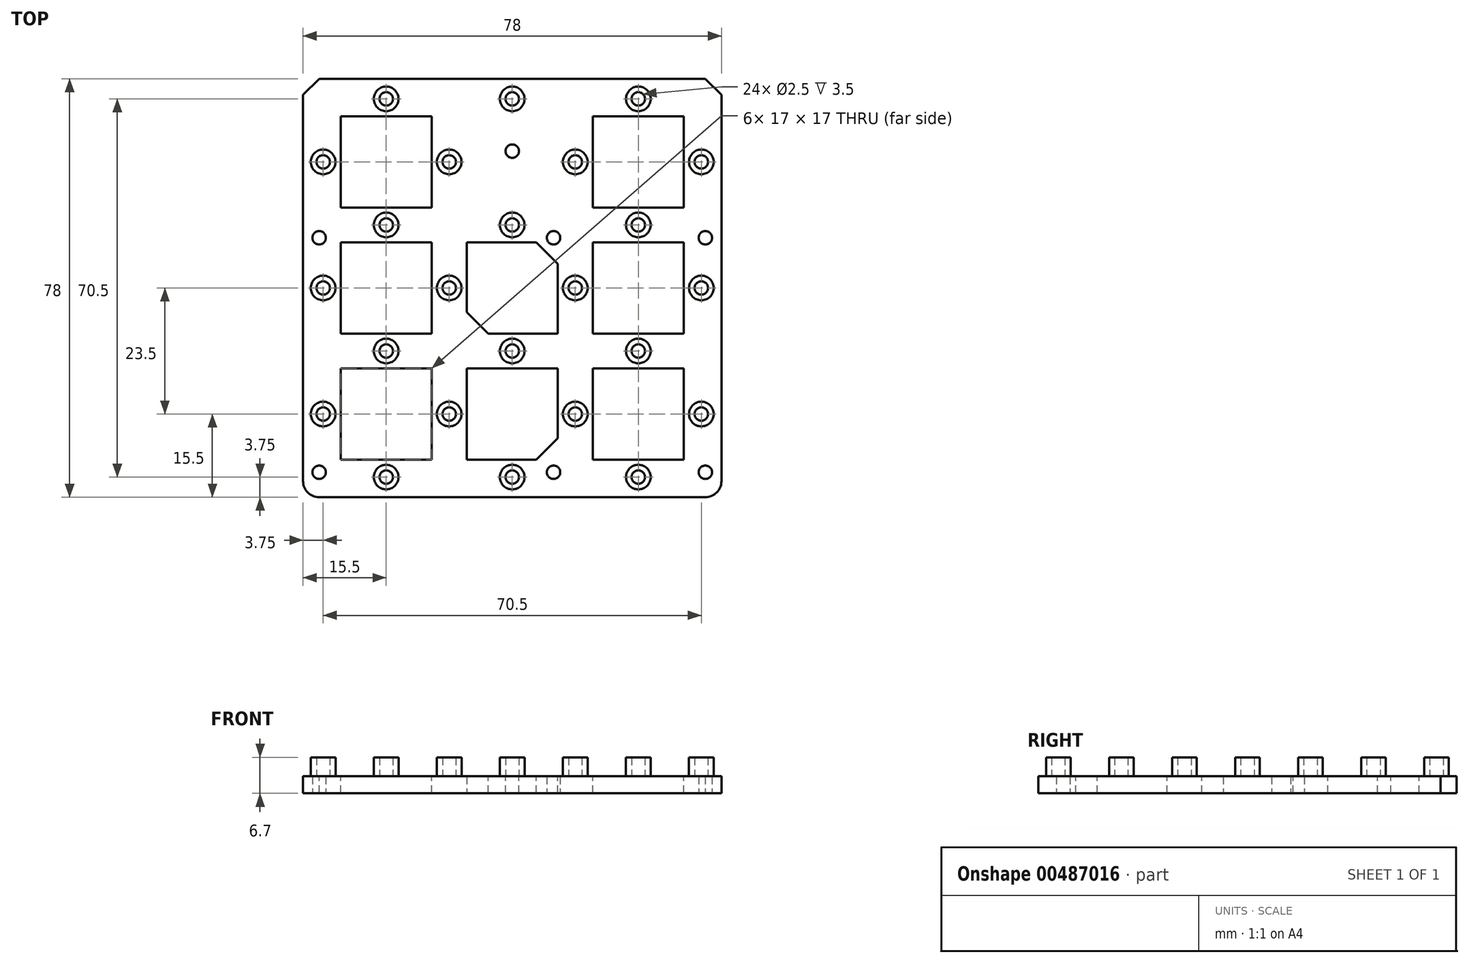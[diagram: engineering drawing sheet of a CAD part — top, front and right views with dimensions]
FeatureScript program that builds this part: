
annotation { "Feature Type Name" : "Feature", "Feature Type Description" : "" }
export const myFeature = defineFeature(function(context is Context, id is Id, definition is map)
    precondition{}
    {
        {
            assignVariable(context, id + "F0", {"name" : "Grosor", "anyValue" : 3.2});
        }
        {
            var Q0;
            Q0=qCreatedBy(makeId("Top.planeOp"),FACE);
            var sketch = newSketch(context, id + "F1", { "sketchPlane" : qUnion([Q0])});
            skLineSegment(sketch, "E0", {"start": v(0, 0) * mm, "end": v(0, 0) * mm});
            skLineSegment(sketch, "E1", {"start": v(0, 0) * mm, "end": v(0, -12.5) * mm, "construction": true});
            skLineSegment(sketch, "E2.bottom", {"start": v(-36, -34.35) * mm, "end": v(36, -34.35) * mm, "construction": true});
            skLineSegment(sketch, "E2.top", {"start": v(-36, 9.35) * mm, "end": v(36, 9.35) * mm, "construction": true});
            skLineSegment(sketch, "E2.left", {"start": v(-36, -34.35) * mm, "end": v(-36, 9.35) * mm, "construction": true});
            skLineSegment(sketch, "E2.right", {"start": v(36, -34.35) * mm, "end": v(36, 9.35) * mm, "construction": true});
            skPoint(sketch, "E2.middle", {"position": v(0, -12.5) * mm});
            skLineSegment(sketch, "E3.bottom", {"start": v(39, 12) * mm, "end": v(-39, 12) * mm, "construction": true});
            skLineSegment(sketch, "E3.top", {"start": v(39, -37) * mm, "end": v(-39, -37) * mm, "construction": true});
            skLineSegment(sketch, "E3.left", {"start": v(39, 12) * mm, "end": v(39, -37) * mm, "construction": true});
            skLineSegment(sketch, "E3.right", {"start": v(-39, 12) * mm, "end": v(-39, -37) * mm, "construction": true});
            skCircle(sketch, "E4", {"center": v(-36, 9.35) * mm, "radius": 1.25 * mm});
            skCircle(sketch, "E5", {"center": v(36, 9.35) * mm, "radius": 1.25 * mm});
            skCircle(sketch, "E6", {"center": v(36, -34.35) * mm, "radius": 1.25 * mm});
            skCircle(sketch, "E7", {"center": v(-36, -34.35) * mm, "radius": 1.25 * mm});
            skCircle(sketch, "E8", {"center": v(-36, -34.35) * mm, "radius": 2.3 * mm});
            skCircle(sketch, "E9", {"center": v(36, -34.35) * mm, "radius": 2.3 * mm});
            skCircle(sketch, "E10", {"center": v(36, 9.35) * mm, "radius": 2.3 * mm});
            skCircle(sketch, "E11", {"center": v(-36, 9.35) * mm, "radius": 2.3 * mm});
            skLineSegment(sketch, "E12.bottom", {"start": v(-39, -39) * mm, "end": v(39, -39) * mm});
            skLineSegment(sketch, "E12.top", {"start": v(-39, 39) * mm, "end": v(39, 39) * mm});
            skLineSegment(sketch, "E12.left", {"start": v(-39, -39) * mm, "end": v(-39, 39) * mm});
            skLineSegment(sketch, "E12.right", {"start": v(39, -39) * mm, "end": v(39, 39) * mm});
            skPoint(sketch, "E12.middle", {"position": v(0, 0) * mm});
            skLineSegment(sketch, "E13", {"start": v(-36, -20.87) * mm, "end": v(7.7, -20.87) * mm, "construction": true});
            skLineSegment(sketch, "E14", {"start": v(7.7, -20.87) * mm, "end": v(7.7, -34.35) * mm, "construction": true});
            skLineSegment(sketch, "E15", {"start": v(7.7, -20.87) * mm, "end": v(7.7, 9.35) * mm, "construction": true});
            skCircle(sketch, "E16", {"center": v(7.7, 9.35) * mm, "radius": 1.25 * mm});
            skCircle(sketch, "E17", {"center": v(7.7, -34.35) * mm, "radius": 1.25 * mm});
            skCircle(sketch, "E18", {"center": v(7.7, -34.35) * mm, "radius": 2.3 * mm});
            skCircle(sketch, "E19", {"center": v(7.7, 9.35) * mm, "radius": 2.3 * mm});
            skLineSegment(sketch, "E20", {"start": v(0, 12) * mm, "end": v(0, 39) * mm, "construction": true});
            skCircle(sketch, "E21", {"center": v(0, 25.5) * mm, "radius": 1.25 * mm});
            skSolve(sketch);
        }
        {
            var Q0;
            Q0=qSketchRegion(id+"F1",true);
            var Q1;
            Q1=makeQuery(id+"F1.imprint","IMPRINT",FACE,{"disambiguationData":[TD([[makeQuery(id+"F1.imprint","IMPRINT",EDGE,{"derivedFrom":sQuery(id+"F1.wireOp",EDGE,"E4")}),-1.0]])]});
            var Q2;
            Q2=makeQuery(id+"F1.imprint","IMPRINT",FACE,{"disambiguationData":[TD([[makeQuery(id+"F1.imprint","IMPRINT",EDGE,{"derivedFrom":sQuery(id+"F1.wireOp",EDGE,"E5")}),-1.0]])]});
            var Q3;
            Q3=makeQuery(id+"F1.imprint","IMPRINT",FACE,{"disambiguationData":[TD([[makeQuery(id+"F1.imprint","IMPRINT",EDGE,{"derivedFrom":sQuery(id+"F1.wireOp",EDGE,"E6")}),-1.0]])]});
            var Q4;
            Q4=makeQuery(id+"F1.imprint","IMPRINT",FACE,{"disambiguationData":[TD([[makeQuery(id+"F1.imprint","IMPRINT",EDGE,{"derivedFrom":sQuery(id+"F1.wireOp",EDGE,"E7")}),-1.0]])]});
            var Q5;
            Q5=makeQuery(id+"F1.imprint","IMPRINT",FACE,{"disambiguationData":[TD([[makeQuery(id+"F1.imprint","IMPRINT",EDGE,{"derivedFrom":sQuery(id+"F1.wireOp",EDGE,"E16")}),-1.0]])]});
            var Q6;
            Q6=makeQuery(id+"F1.imprint","IMPRINT",FACE,{"disambiguationData":[TD([[makeQuery(id+"F1.imprint","IMPRINT",EDGE,{"derivedFrom":sQuery(id+"F1.wireOp",EDGE,"E17")}),-1.0]])]});
            var Q7;
            Q7=makeQuery(id+"F1.imprint","IMPRINT",FACE,{"disambiguationData":[TD([[makeQuery(id+"F1.imprint","IMPRINT",EDGE,{"derivedFrom":sQuery(id+"F1.wireOp",EDGE,"E4")}),1.0]])]});
            var Q8;
            Q8=makeQuery(id+"F1.imprint","IMPRINT",FACE,{"disambiguationData":[TD([[makeQuery(id+"F1.imprint","IMPRINT",EDGE,{"derivedFrom":sQuery(id+"F1.wireOp",EDGE,"E16")}),1.0]])]});
            var Q9;
            Q9=makeQuery(id+"F1.imprint","IMPRINT",FACE,{"disambiguationData":[TD([[makeQuery(id+"F1.imprint","IMPRINT",EDGE,{"derivedFrom":sQuery(id+"F1.wireOp",EDGE,"E5")}),1.0]])]});
            var Q10;
            Q10=makeQuery(id+"F1.imprint","IMPRINT",FACE,{"disambiguationData":[TD([[makeQuery(id+"F1.imprint","IMPRINT",EDGE,{"derivedFrom":sQuery(id+"F1.wireOp",EDGE,"E7")}),1.0]])]});
            var Q11;
            Q11=makeQuery(id+"F1.imprint","IMPRINT",FACE,{"disambiguationData":[TD([[makeQuery(id+"F1.imprint","IMPRINT",EDGE,{"derivedFrom":sQuery(id+"F1.wireOp",EDGE,"E17")}),1.0]])]});
            var Q12;
            Q12=makeQuery(id+"F1.imprint","IMPRINT",FACE,{"disambiguationData":[TD([[makeQuery(id+"F1.imprint","IMPRINT",EDGE,{"derivedFrom":sQuery(id+"F1.wireOp",EDGE,"E6")}),1.0]])]});
            extrude(context, id + "F2", {"entities" : qUnion([Q0, Q1, Q2, Q3, Q4, Q5, Q6, Q7, Q8, Q9, Q10, Q11, Q12]), "endBound" : BoundingType.SYMMETRIC, "oppositeDirection" : true, "depth" : (getVariable(context, 'Grosor')) * mm});
        }
        {
            var Q0;
            Q0=qCreatedBy(makeId("Top.planeOp"),FACE);
            var sketch = newSketch(context, id + "F3", { "sketchPlane" : qUnion([Q0])});
            skLineSegment(sketch, "E22", {"start": v(0, 0) * mm, "end": v(-11.75, 0) * mm, "construction": true});
            skLineSegment(sketch, "E23", {"start": v(-11.75, 0) * mm, "end": v(-35.25, 0) * mm, "construction": true});
            skLineSegment(sketch, "E24.bottom", {"start": v(0, 11.75) * mm, "end": v(-23.5, 11.75) * mm, "construction": true});
            skLineSegment(sketch, "E24.top", {"start": v(0, -11.75) * mm, "end": v(-23.5, -11.75) * mm, "construction": true});
            skLineSegment(sketch, "E24.left", {"start": v(0, 11.75) * mm, "end": v(0, -11.75) * mm, "construction": true});
            skLineSegment(sketch, "E24.right", {"start": v(-23.5, 11.75) * mm, "end": v(-23.5, -11.75) * mm, "construction": true});
            skPoint(sketch, "E24.middle", {"position": v(-11.75, 0) * mm});
            skLineSegment(sketch, "E25", {"start": v(0, 0) * mm, "end": v(11.75, 0) * mm, "construction": true});
            skLineSegment(sketch, "E26.bottom", {"start": v(0, -11.75) * mm, "end": v(23.5, -11.75) * mm, "construction": true});
            skLineSegment(sketch, "E26.top", {"start": v(0, 11.75) * mm, "end": v(23.5, 11.75) * mm, "construction": true});
            skLineSegment(sketch, "E26.left", {"start": v(0, -11.75) * mm, "end": v(0, 11.75) * mm, "construction": true});
            skLineSegment(sketch, "E26.right", {"start": v(23.5, -11.75) * mm, "end": v(23.5, 11.75) * mm, "construction": true});
            skPoint(sketch, "E26.middle", {"position": v(11.75, 0) * mm});
            skLineSegment(sketch, "E27.bottom", {"start": v(11.75, 11.75) * mm, "end": v(35.25, 11.75) * mm, "construction": true});
            skLineSegment(sketch, "E27.top", {"start": v(11.75, -11.75) * mm, "end": v(35.25, -11.75) * mm, "construction": true});
            skLineSegment(sketch, "E27.left", {"start": v(11.75, 11.75) * mm, "end": v(11.75, -11.75) * mm, "construction": true});
            skLineSegment(sketch, "E27.right", {"start": v(35.25, 11.75) * mm, "end": v(35.25, -11.75) * mm, "construction": true});
            skPoint(sketch, "E27.middle", {"position": v(23.5, 0) * mm});
            skLineSegment(sketch, "E28", {"start": v(0, -11.75) * mm, "end": v(0, -23.5) * mm, "construction": true});
            skLineSegment(sketch, "E29.bottom", {"start": v(11.75, -11.75) * mm, "end": v(-11.75, -11.75) * mm, "construction": true});
            skLineSegment(sketch, "E29.top", {"start": v(11.75, -35.25) * mm, "end": v(-11.75, -35.25) * mm, "construction": true});
            skLineSegment(sketch, "E29.left", {"start": v(11.75, -11.75) * mm, "end": v(11.75, -35.25) * mm, "construction": true});
            skLineSegment(sketch, "E29.right", {"start": v(-11.75, -11.75) * mm, "end": v(-11.75, -35.25) * mm, "construction": true});
            skPoint(sketch, "E29.middle", {"position": v(0, -23.5) * mm});
            skLineSegment(sketch, "E30.bottom", {"start": v(-23.5, -11.75) * mm, "end": v(0, -11.75) * mm, "construction": true});
            skLineSegment(sketch, "E30.top", {"start": v(-23.5, -35.25) * mm, "end": v(0, -35.25) * mm, "construction": true});
            skLineSegment(sketch, "E30.left", {"start": v(-23.5, -11.75) * mm, "end": v(-23.5, -35.25) * mm, "construction": true});
            skLineSegment(sketch, "E30.right", {"start": v(0, -11.75) * mm, "end": v(0, -35.25) * mm, "construction": true});
            skPoint(sketch, "E30.middle", {"position": v(-11.75, -23.5) * mm});
            skLineSegment(sketch, "E31.bottom", {"start": v(-11.75, -11.75) * mm, "end": v(-35.25, -11.75) * mm, "construction": true});
            skLineSegment(sketch, "E31.top", {"start": v(-11.75, -35.25) * mm, "end": v(-35.25, -35.25) * mm, "construction": true});
            skLineSegment(sketch, "E31.right", {"start": v(-35.25, -11.75) * mm, "end": v(-35.25, -35.25) * mm, "construction": true});
            skPoint(sketch, "E31.middle", {"position": v(-23.5, -23.5) * mm});
            skLineSegment(sketch, "E32.bottom", {"start": v(23.5, -11.75) * mm, "end": v(0, -11.75) * mm, "construction": true});
            skLineSegment(sketch, "E32.top", {"start": v(23.5, -35.25) * mm, "end": v(0, -35.25) * mm, "construction": true});
            skLineSegment(sketch, "E32.left", {"start": v(23.5, -11.75) * mm, "end": v(23.5, -35.25) * mm, "construction": true});
            skPoint(sketch, "E32.middle", {"position": v(11.75, -23.5) * mm});
            skLineSegment(sketch, "E33.bottom", {"start": v(35.25, -11.75) * mm, "end": v(11.75, -11.75) * mm, "construction": true});
            skLineSegment(sketch, "E33.top", {"start": v(35.25, -35.25) * mm, "end": v(11.75, -35.25) * mm, "construction": true});
            skLineSegment(sketch, "E33.left", {"start": v(35.25, -11.75) * mm, "end": v(35.25, -35.25) * mm, "construction": true});
            skPoint(sketch, "E33.middle", {"position": v(23.5, -23.5) * mm});
            skLineSegment(sketch, "E34", {"start": v(0, 11.75) * mm, "end": v(0, 23.5) * mm, "construction": true});
            skLineSegment(sketch, "E35.bottom", {"start": v(11.75, 11.75) * mm, "end": v(-11.75, 11.75) * mm, "construction": true});
            skLineSegment(sketch, "E35.top", {"start": v(11.75, 35.25) * mm, "end": v(-11.75, 35.25) * mm, "construction": true});
            skLineSegment(sketch, "E35.left", {"start": v(11.75, 11.75) * mm, "end": v(11.75, 35.25) * mm, "construction": true});
            skLineSegment(sketch, "E35.right", {"start": v(-11.75, 11.75) * mm, "end": v(-11.75, 35.25) * mm, "construction": true});
            skPoint(sketch, "E35.middle", {"position": v(0, 23.5) * mm});
            skLineSegment(sketch, "E36.top", {"start": v(11.75, 35.25) * mm, "end": v(35.25, 35.25) * mm, "construction": true});
            skLineSegment(sketch, "E36.right", {"start": v(35.25, 11.75) * mm, "end": v(35.25, 35.25) * mm, "construction": true});
            skPoint(sketch, "E36.middle", {"position": v(23.5, 23.5) * mm});
            skPoint(sketch, "E36.middle.positionSnap0", {"position": v(11.75, 23.5) * mm});
            skPoint(sketch, "E36.centerSnap0", {"position": v(11.75, 23.5) * mm});
            skLineSegment(sketch, "E37", {"start": v(-11.75, 23.5) * mm, "end": v(-35.25, 23.5) * mm, "construction": true});
            skLineSegment(sketch, "E38", {"start": v(-23.5, 11.75) * mm, "end": v(-23.5, 35.25) * mm, "construction": true});
            skCircle(sketch, "E39", {"center": v(-11.75, 0) * mm, "radius": 2.3 * mm});
            skCircle(sketch, "E40", {"center": v(0, 11.75) * mm, "radius": 2.3 * mm});
            skCircle(sketch, "E41", {"center": v(11.75, 0) * mm, "radius": 1.25 * mm});
            skCircle(sketch, "E42", {"center": v(0, -11.75) * mm, "radius": 2.3 * mm});
            skCircle(sketch, "E43", {"center": v(-11.75, -23.5) * mm, "radius": 1.25 * mm});
            skCircle(sketch, "E44", {"center": v(-35.25, -23.5) * mm, "radius": 2.3 * mm});
            skCircle(sketch, "E45", {"center": v(11.75, -23.5) * mm, "radius": 2.3 * mm});
            skCircle(sketch, "E46", {"center": v(35.25, -23.5) * mm, "radius": 1.25 * mm});
            skCircle(sketch, "E47", {"center": v(35.25, 0) * mm, "radius": 1.25 * mm});
            skCircle(sketch, "E48", {"center": v(23.5, -11.75) * mm, "radius": 1.25 * mm});
            skCircle(sketch, "E49", {"center": v(-23.5, -11.75) * mm, "radius": 2.3 * mm});
            skCircle(sketch, "E50", {"center": v(-35.25, 0) * mm, "radius": 1.25 * mm});
            skCircle(sketch, "E51", {"center": v(-35.25, 23.5) * mm, "radius": 1.25 * mm});
            skCircle(sketch, "E52", {"center": v(-23.5, 35.25) * mm, "radius": 2.3 * mm});
            skCircle(sketch, "E53", {"center": v(-23.5, 11.75) * mm, "radius": 1.25 * mm});
            skCircle(sketch, "E54", {"center": v(-11.75, 23.5) * mm, "radius": 2.3 * mm});
            skCircle(sketch, "E55", {"center": v(11.75, 23.5) * mm, "radius": 1.25 * mm});
            skCircle(sketch, "E56", {"center": v(35.25, 23.5) * mm, "radius": 1.25 * mm});
            skCircle(sketch, "E57", {"center": v(23.5, 11.75) * mm, "radius": 1.25 * mm});
            skCircle(sketch, "E58", {"center": v(23.5, 35.25) * mm, "radius": 2.3 * mm});
            skCircle(sketch, "E59", {"center": v(0, 35.25) * mm, "radius": 2.3 * mm});
            skCircle(sketch, "E60", {"center": v(-23.5, -35.25) * mm, "radius": 1.25 * mm});
            skCircle(sketch, "E61", {"center": v(0, -35.25) * mm, "radius": 1.25 * mm});
            skCircle(sketch, "E62", {"center": v(23.5, -35.25) * mm, "radius": 2.3 * mm});
            skCircle(sketch, "E63", {"center": v(-23.5, 35.25) * mm, "radius": 1.25 * mm});
            skCircle(sketch, "E64", {"center": v(-35.25, 23.5) * mm, "radius": 2.3 * mm});
            skCircle(sketch, "E65", {"center": v(-23.5, 11.75) * mm, "radius": 2.3 * mm});
            skCircle(sketch, "E66", {"center": v(-35.25, 0) * mm, "radius": 2.3 * mm});
            skCircle(sketch, "E67", {"center": v(-23.5, -11.75) * mm, "radius": 1.25 * mm});
            skCircle(sketch, "E68", {"center": v(-11.75, 0) * mm, "radius": 1.25 * mm});
            skCircle(sketch, "E69", {"center": v(-35.25, -23.5) * mm, "radius": 1.25 * mm});
            skCircle(sketch, "E70", {"center": v(-11.75, -23.5) * mm, "radius": 2.3 * mm});
            skCircle(sketch, "E71", {"center": v(-23.5, -35.25) * mm, "radius": 2.3 * mm});
            skCircle(sketch, "E72", {"center": v(0, -35.25) * mm, "radius": 2.3 * mm});
            skCircle(sketch, "E73", {"center": v(-11.75, 23.5) * mm, "radius": 1.25 * mm});
            skCircle(sketch, "E74", {"center": v(0, 35.25) * mm, "radius": 1.25 * mm});
            skCircle(sketch, "E75", {"center": v(0, 11.75) * mm, "radius": 1.25 * mm});
            skCircle(sketch, "E76", {"center": v(0, -11.75) * mm, "radius": 1.25 * mm});
            skCircle(sketch, "E77", {"center": v(11.75, 0) * mm, "radius": 2.3 * mm});
            skCircle(sketch, "E78", {"center": v(11.75, -23.5) * mm, "radius": 1.25 * mm});
            skCircle(sketch, "E79", {"center": v(23.5, -11.75) * mm, "radius": 2.3 * mm});
            skCircle(sketch, "E80", {"center": v(35.25, 0) * mm, "radius": 2.3 * mm});
            skCircle(sketch, "E81", {"center": v(23.5, 11.75) * mm, "radius": 2.3 * mm});
            skCircle(sketch, "E82", {"center": v(11.75, 23.5) * mm, "radius": 2.3 * mm});
            skCircle(sketch, "E83", {"center": v(35.25, 23.5) * mm, "radius": 2.3 * mm});
            skCircle(sketch, "E84", {"center": v(35.25, -23.5) * mm, "radius": 2.3 * mm});
            skCircle(sketch, "E85", {"center": v(23.5, -35.25) * mm, "radius": 1.25 * mm});
            skCircle(sketch, "E86", {"center": v(23.5, 35.25) * mm, "radius": 1.25 * mm});
            skLineSegment(sketch, "E87.bottom", {"start": v(-8.5, -8.5) * mm, "end": v(8.5, -8.5) * mm});
            skLineSegment(sketch, "E87.top", {"start": v(-8.5, 8.5) * mm, "end": v(8.5, 8.5) * mm});
            skLineSegment(sketch, "E87.left", {"start": v(-8.5, -8.5) * mm, "end": v(-8.5, 8.5) * mm});
            skLineSegment(sketch, "E87.right", {"start": v(8.5, -8.5) * mm, "end": v(8.5, 8.5) * mm});
            skPoint(sketch, "E87.middle", {"position": v(0, 0) * mm});
            skLineSegment(sketch, "E88.bottom", {"start": v(-32, -8.5) * mm, "end": v(-15, -8.5) * mm});
            skLineSegment(sketch, "E88.top", {"start": v(-32, 8.5) * mm, "end": v(-15, 8.5) * mm});
            skLineSegment(sketch, "E88.left", {"start": v(-32, -8.5) * mm, "end": v(-32, 8.5) * mm});
            skLineSegment(sketch, "E88.right", {"start": v(-15, -8.5) * mm, "end": v(-15, 8.5) * mm});
            skPoint(sketch, "E88.middle", {"position": v(-23.5, 0) * mm});
            skLineSegment(sketch, "E89.bottom", {"start": v(15, -8.5) * mm, "end": v(32, -8.5) * mm});
            skLineSegment(sketch, "E89.top", {"start": v(15, 8.5) * mm, "end": v(32, 8.5) * mm});
            skLineSegment(sketch, "E89.left", {"start": v(15, -8.5) * mm, "end": v(15, 8.5) * mm});
            skLineSegment(sketch, "E89.right", {"start": v(32, -8.5) * mm, "end": v(32, 8.5) * mm});
            skLineSegment(sketch, "E90.bottom", {"start": v(15, 15) * mm, "end": v(32, 15) * mm});
            skLineSegment(sketch, "E90.top", {"start": v(15, 32) * mm, "end": v(32, 32) * mm});
            skLineSegment(sketch, "E90.left", {"start": v(15, 15) * mm, "end": v(15, 32) * mm});
            skLineSegment(sketch, "E90.right", {"start": v(32, 15) * mm, "end": v(32, 32) * mm});
            skLineSegment(sketch, "E91.bottom", {"start": v(-8.5, 32) * mm, "end": v(8.5, 32) * mm});
            skLineSegment(sketch, "E91.top", {"start": v(-8.5, 15) * mm, "end": v(8.5, 15) * mm});
            skLineSegment(sketch, "E91.left", {"start": v(-8.5, 32) * mm, "end": v(-8.5, 15) * mm});
            skLineSegment(sketch, "E91.right", {"start": v(8.5, 32) * mm, "end": v(8.5, 15) * mm});
            skLineSegment(sketch, "E92.bottom", {"start": v(-32, -15) * mm, "end": v(-15, -15) * mm});
            skLineSegment(sketch, "E92.top", {"start": v(-32, -32) * mm, "end": v(-15, -32) * mm});
            skLineSegment(sketch, "E92.left", {"start": v(-32, -15) * mm, "end": v(-32, -32) * mm});
            skLineSegment(sketch, "E92.right", {"start": v(-15, -15) * mm, "end": v(-15, -32) * mm});
            skLineSegment(sketch, "E93.bottom", {"start": v(-8.5, -32) * mm, "end": v(8.5, -32) * mm});
            skLineSegment(sketch, "E93.top", {"start": v(-8.5, -15) * mm, "end": v(8.5, -15) * mm});
            skLineSegment(sketch, "E93.left", {"start": v(-8.5, -32) * mm, "end": v(-8.5, -15) * mm});
            skLineSegment(sketch, "E93.right", {"start": v(8.5, -32) * mm, "end": v(8.5, -15) * mm});
            skLineSegment(sketch, "E94.bottom", {"start": v(15, -32) * mm, "end": v(32, -32) * mm});
            skLineSegment(sketch, "E94.top", {"start": v(15, -15) * mm, "end": v(32, -15) * mm});
            skLineSegment(sketch, "E94.left", {"start": v(15, -32) * mm, "end": v(15, -15) * mm});
            skLineSegment(sketch, "E94.right", {"start": v(32, -32) * mm, "end": v(32, -15) * mm});
            skLineSegment(sketch, "E95.bottom", {"start": v(-15, 15) * mm, "end": v(-32, 15) * mm});
            skLineSegment(sketch, "E95.top", {"start": v(-15, 32) * mm, "end": v(-32, 32) * mm});
            skLineSegment(sketch, "E95.left", {"start": v(-15, 15) * mm, "end": v(-15, 32) * mm});
            skLineSegment(sketch, "E95.right", {"start": v(-32, 15) * mm, "end": v(-32, 32) * mm});
            skPoint(sketch, "E95.middle", {"position": v(-23.5, 23.5) * mm});
            skSolve(sketch);
        }
        {
            var Q0;
            Q0=makeQuery(id+"F3.imprint","IMPRINT",FACE,{"disambiguationData":[TD([[makeQuery(id+"F3.imprint","IMPRINT",EDGE,{"derivedFrom":sQuery(id+"F3.wireOp",EDGE,"E87.bottom")}),1.0]])]});
            var Q1;
            Q1=makeQuery(id+"F3.imprint","IMPRINT",FACE,{"disambiguationData":[TD([[makeQuery(id+"F3.imprint","IMPRINT",EDGE,{"derivedFrom":sQuery(id+"F3.wireOp",EDGE,"E88.bottom")}),1.0]])]});
            var Q2;
            Q2=makeQuery(id+"F3.imprint","IMPRINT",FACE,{"disambiguationData":[TD([[makeQuery(id+"F3.imprint","IMPRINT",EDGE,{"derivedFrom":sQuery(id+"F3.wireOp",EDGE,"E89.bottom")}),1.0]])]});
            var Q3;
            Q3=makeQuery(id+"F3.imprint","IMPRINT",FACE,{"disambiguationData":[TD([[makeQuery(id+"F3.imprint","IMPRINT",EDGE,{"derivedFrom":sQuery(id+"F3.wireOp",EDGE,"E90.bottom")}),1.0]])]});
            var Q4;
            Q4=makeQuery(id+"F3.imprint","IMPRINT",FACE,{"disambiguationData":[TD([[makeQuery(id+"F3.imprint","IMPRINT",EDGE,{"derivedFrom":sQuery(id+"F3.wireOp",EDGE,"E92.bottom")}),-1.0]])]});
            var Q5;
            Q5=makeQuery(id+"F3.imprint","IMPRINT",FACE,{"disambiguationData":[TD([[makeQuery(id+"F3.imprint","IMPRINT",EDGE,{"derivedFrom":sQuery(id+"F3.wireOp",EDGE,"E93.bottom")}),1.0]])]});
            var Q6;
            Q6=makeQuery(id+"F3.imprint","IMPRINT",FACE,{"disambiguationData":[TD([[makeQuery(id+"F3.imprint","IMPRINT",EDGE,{"derivedFrom":sQuery(id+"F3.wireOp",EDGE,"E94.bottom")}),1.0]])]});
            var Q7;
            Q7=makeQuery(id+"F3.imprint","IMPRINT",FACE,{"disambiguationData":[TD([[makeQuery(id+"F3.imprint","IMPRINT",EDGE,{"derivedFrom":sQuery(id+"F3.wireOp",EDGE,"E95.bottom")}),-1.0]])]});
            var Q8;
            Q8=makeQuery(id+"F3.imprint","IMPRINT",FACE,{"disambiguationData":[TD([[makeQuery(id+"F3.imprint","IMPRINT",EDGE,{"derivedFrom":sQuery(id+"F3.wireOp",EDGE,"E39")}),1.0]])]});
            var Q9;
            Q9=makeQuery(id+"F3.imprint","IMPRINT",FACE,{"disambiguationData":[TD([[makeQuery(id+"F3.imprint","IMPRINT",EDGE,{"derivedFrom":sQuery(id+"F3.wireOp",EDGE,"E40")}),1.0]])]});
            var Q10;
            Q10=makeQuery(id+"F3.imprint","IMPRINT",FACE,{"disambiguationData":[TD([[makeQuery(id+"F3.imprint","IMPRINT",EDGE,{"derivedFrom":sQuery(id+"F3.wireOp",EDGE,"E41")}),-1.0]])]});
            var Q11;
            Q11=makeQuery(id+"F3.imprint","IMPRINT",FACE,{"disambiguationData":[TD([[makeQuery(id+"F3.imprint","IMPRINT",EDGE,{"derivedFrom":sQuery(id+"F3.wireOp",EDGE,"E42")}),1.0]])]});
            var Q12;
            Q12=makeQuery(id+"F3.imprint","IMPRINT",FACE,{"disambiguationData":[TD([[makeQuery(id+"F3.imprint","IMPRINT",EDGE,{"derivedFrom":sQuery(id+"F3.wireOp",EDGE,"E43")}),-1.0]])]});
            var Q13;
            Q13=makeQuery(id+"F3.imprint","IMPRINT",FACE,{"disambiguationData":[TD([[makeQuery(id+"F3.imprint","IMPRINT",EDGE,{"derivedFrom":sQuery(id+"F3.wireOp",EDGE,"E44")}),1.0]])]});
            var Q14;
            Q14=makeQuery(id+"F3.imprint","IMPRINT",FACE,{"disambiguationData":[TD([[makeQuery(id+"F3.imprint","IMPRINT",EDGE,{"derivedFrom":sQuery(id+"F3.wireOp",EDGE,"E45")}),1.0]])]});
            var Q15;
            Q15=makeQuery(id+"F3.imprint","IMPRINT",FACE,{"disambiguationData":[TD([[makeQuery(id+"F3.imprint","IMPRINT",EDGE,{"derivedFrom":sQuery(id+"F3.wireOp",EDGE,"E46")}),-1.0]])]});
            var Q16;
            Q16=makeQuery(id+"F3.imprint","IMPRINT",FACE,{"disambiguationData":[TD([[makeQuery(id+"F3.imprint","IMPRINT",EDGE,{"derivedFrom":sQuery(id+"F3.wireOp",EDGE,"E47")}),-1.0]])]});
            var Q17;
            Q17=makeQuery(id+"F3.imprint","IMPRINT",FACE,{"disambiguationData":[TD([[makeQuery(id+"F3.imprint","IMPRINT",EDGE,{"derivedFrom":sQuery(id+"F3.wireOp",EDGE,"E48")}),-1.0]])]});
            var Q18;
            Q18=makeQuery(id+"F3.imprint","IMPRINT",FACE,{"disambiguationData":[TD([[makeQuery(id+"F3.imprint","IMPRINT",EDGE,{"derivedFrom":sQuery(id+"F3.wireOp",EDGE,"E49")}),1.0]])]});
            var Q19;
            Q19=makeQuery(id+"F3.imprint","IMPRINT",FACE,{"disambiguationData":[TD([[makeQuery(id+"F3.imprint","IMPRINT",EDGE,{"derivedFrom":sQuery(id+"F3.wireOp",EDGE,"E50")}),-1.0]])]});
            var Q20;
            Q20=makeQuery(id+"F3.imprint","IMPRINT",FACE,{"disambiguationData":[TD([[makeQuery(id+"F3.imprint","IMPRINT",EDGE,{"derivedFrom":sQuery(id+"F3.wireOp",EDGE,"E51")}),-1.0]])]});
            var Q21;
            Q21=makeQuery(id+"F3.imprint","IMPRINT",FACE,{"disambiguationData":[TD([[makeQuery(id+"F3.imprint","IMPRINT",EDGE,{"derivedFrom":sQuery(id+"F3.wireOp",EDGE,"E52")}),1.0]])]});
            var Q22;
            Q22=makeQuery(id+"F3.imprint","IMPRINT",FACE,{"disambiguationData":[TD([[makeQuery(id+"F3.imprint","IMPRINT",EDGE,{"derivedFrom":sQuery(id+"F3.wireOp",EDGE,"E53")}),-1.0]])]});
            var Q23;
            Q23=makeQuery(id+"F3.imprint","IMPRINT",FACE,{"disambiguationData":[TD([[makeQuery(id+"F3.imprint","IMPRINT",EDGE,{"derivedFrom":sQuery(id+"F3.wireOp",EDGE,"E54")}),1.0]])]});
            var Q24;
            Q24=makeQuery(id+"F3.imprint","IMPRINT",FACE,{"disambiguationData":[TD([[makeQuery(id+"F3.imprint","IMPRINT",EDGE,{"derivedFrom":sQuery(id+"F3.wireOp",EDGE,"E55")}),-1.0]])]});
            var Q25;
            Q25=makeQuery(id+"F3.imprint","IMPRINT",FACE,{"disambiguationData":[TD([[makeQuery(id+"F3.imprint","IMPRINT",EDGE,{"derivedFrom":sQuery(id+"F3.wireOp",EDGE,"E56")}),-1.0]])]});
            var Q26;
            Q26=makeQuery(id+"F3.imprint","IMPRINT",FACE,{"disambiguationData":[TD([[makeQuery(id+"F3.imprint","IMPRINT",EDGE,{"derivedFrom":sQuery(id+"F3.wireOp",EDGE,"E57")}),-1.0]])]});
            var Q27;
            Q27=makeQuery(id+"F3.imprint","IMPRINT",FACE,{"disambiguationData":[TD([[makeQuery(id+"F3.imprint","IMPRINT",EDGE,{"derivedFrom":sQuery(id+"F3.wireOp",EDGE,"E58")}),1.0]])]});
            var Q28;
            Q28=makeQuery(id+"F3.imprint","IMPRINT",FACE,{"disambiguationData":[TD([[makeQuery(id+"F3.imprint","IMPRINT",EDGE,{"derivedFrom":sQuery(id+"F3.wireOp",EDGE,"E59")}),1.0]])]});
            var Q29;
            Q29=makeQuery(id+"F3.imprint","IMPRINT",FACE,{"disambiguationData":[TD([[makeQuery(id+"F3.imprint","IMPRINT",EDGE,{"derivedFrom":sQuery(id+"F3.wireOp",EDGE,"E60")}),-1.0]])]});
            var Q30;
            Q30=makeQuery(id+"F3.imprint","IMPRINT",FACE,{"disambiguationData":[TD([[makeQuery(id+"F3.imprint","IMPRINT",EDGE,{"derivedFrom":sQuery(id+"F3.wireOp",EDGE,"E61")}),-1.0]])]});
            var Q31;
            Q31=makeQuery(id+"F3.imprint","IMPRINT",FACE,{"disambiguationData":[TD([[makeQuery(id+"F3.imprint","IMPRINT",EDGE,{"derivedFrom":sQuery(id+"F3.wireOp",EDGE,"E62")}),1.0]])]});
            extrude(context, id + "F4", {"entities" : qUnion([Q0, Q1, Q2, Q3, Q4, Q5, Q6, Q7, Q8, Q9, Q10, Q11, Q12, Q13, Q14, Q15, Q16, Q17, Q18, Q19, Q20, Q21, Q22, Q23, Q24, Q25, Q26, Q27, Q28, Q29, Q30, Q31]), "operationType" : NewBodyOperationType.ADD, "depth" : (getVariable(context, 'Grosor') / 2 + 3.5) * mm});
        }
        {
            var Q0;
            Q0=makeQuery(id+"F3.imprint","IMPRINT",FACE,{"disambiguationData":[TD([[makeQuery(id+"F3.imprint","IMPRINT",EDGE,{"derivedFrom":sQuery(id+"F3.wireOp",EDGE,"E95.bottom")}),-1.0]])]});
            var Q1;
            Q1=makeQuery(id+"F3.imprint","IMPRINT",FACE,{"disambiguationData":[TD([[makeQuery(id+"F3.imprint","IMPRINT",EDGE,{"derivedFrom":sQuery(id+"F3.wireOp",EDGE,"E90.bottom")}),1.0]])]});
            var Q2;
            Q2=makeQuery(id+"F3.imprint","IMPRINT",FACE,{"disambiguationData":[TD([[makeQuery(id+"F3.imprint","IMPRINT",EDGE,{"derivedFrom":sQuery(id+"F3.wireOp",EDGE,"E89.bottom")}),1.0]])]});
            var Q3;
            Q3=makeQuery(id+"F3.imprint","IMPRINT",FACE,{"disambiguationData":[TD([[makeQuery(id+"F3.imprint","IMPRINT",EDGE,{"derivedFrom":sQuery(id+"F3.wireOp",EDGE,"E87.bottom")}),1.0]])]});
            var Q4;
            Q4=makeQuery(id+"F3.imprint","IMPRINT",FACE,{"disambiguationData":[TD([[makeQuery(id+"F3.imprint","IMPRINT",EDGE,{"derivedFrom":sQuery(id+"F3.wireOp",EDGE,"E88.bottom")}),1.0]])]});
            var Q5;
            Q5=makeQuery(id+"F3.imprint","IMPRINT",FACE,{"disambiguationData":[TD([[makeQuery(id+"F3.imprint","IMPRINT",EDGE,{"derivedFrom":sQuery(id+"F3.wireOp",EDGE,"E92.bottom")}),-1.0]])]});
            var Q6;
            Q6=makeQuery(id+"F3.imprint","IMPRINT",FACE,{"disambiguationData":[TD([[makeQuery(id+"F3.imprint","IMPRINT",EDGE,{"derivedFrom":sQuery(id+"F3.wireOp",EDGE,"E93.bottom")}),1.0]])]});
            var Q7;
            Q7=makeQuery(id+"F3.imprint","IMPRINT",FACE,{"disambiguationData":[TD([[makeQuery(id+"F3.imprint","IMPRINT",EDGE,{"derivedFrom":sQuery(id+"F3.wireOp",EDGE,"E94.bottom")}),1.0]])]});
            extrude(context, id + "F5", {"entities" : qUnion([Q0, Q1, Q2, Q3, Q4, Q5, Q6, Q7]), "operationType" : NewBodyOperationType.REMOVE, "endBound" : BoundingType.SYMMETRIC, "oppositeDirection" : true, "depth" : 20 * mm});
        }
        {
            var Q0;
            Q0=makeQuery(id+"F2.opExtrude","SWEPT_EDGE",EDGE,{"disambiguationData":[OSD([sQuery(id+"F1.wireOp",EDGE,"E12.top"),sQuery(id+"F1.wireOp",EDGE,"E12.right")])]});
            var Q1;
            Q1=makeQuery(id+"F2.opExtrude","SWEPT_EDGE",EDGE,{"disambiguationData":[OSD([sQuery(id+"F1.wireOp",EDGE,"E12.top"),sQuery(id+"F1.wireOp",EDGE,"E12.left")])]});
            chamfer(context, id + "F6", {"entities" : qUnion([Q0, Q1]), "width" : 3 * mm, "tangentPropagation" : true});
        }
        {
            var Q0;
            Q0=makeQuery(id+"F2.opExtrude","SWEPT_EDGE",EDGE,{"disambiguationData":[OSD([sQuery(id+"F1.wireOp",EDGE,"E12.bottom"),sQuery(id+"F1.wireOp",EDGE,"E12.left")])]});
            var Q1;
            Q1=makeQuery(id+"F2.opExtrude","SWEPT_EDGE",EDGE,{"disambiguationData":[OSD([sQuery(id+"F1.wireOp",EDGE,"E12.bottom"),sQuery(id+"F1.wireOp",EDGE,"E12.right")])]});
            fillet(context, id + "F7", {"entities" : qUnion([Q0, Q1]), "radius" : 3 * mm, "tangentPropagation" : true, "allowEdgeOverflow" : false});
        }
        {
            var Q0;
            Q0=makeQuery(id+"F5.boolean.opBoolean","COPY",EDGE,{"derivedFrom":makeQuery(id+"F5.opExtrude","SWEPT_EDGE",EDGE,{"disambiguationData":[OSD([sQuery(id+"F3.wireOp",EDGE,"E87.top"),sQuery(id+"F3.wireOp",EDGE,"E87.right")])]})});
            var Q1;
            Q1=makeQuery(id+"F5.boolean.opBoolean","COPY",EDGE,{"derivedFrom":makeQuery(id+"F5.opExtrude","SWEPT_EDGE",EDGE,{"disambiguationData":[OSD([sQuery(id+"F3.wireOp",EDGE,"E87.bottom"),sQuery(id+"F3.wireOp",EDGE,"E87.left")])]})});
            var Q2;
            Q2=makeQuery(id+"F5.boolean.opBoolean","COPY",EDGE,{"derivedFrom":makeQuery(id+"F5.opExtrude","SWEPT_EDGE",EDGE,{"disambiguationData":[OSD([sQuery(id+"F3.wireOp",EDGE,"E93.bottom"),sQuery(id+"F3.wireOp",EDGE,"E93.right")])]})});
            chamfer(context, id + "F8", {"entities" : qUnion([Q0, Q1, Q2]), "width" : 4 * mm, "tangentPropagation" : true});
        }
        {
            var Q0;
            Q0=makeQuery(id+"F1.imprint","IMPRINT",FACE,{"disambiguationData":[TD([[makeQuery(id+"F1.imprint","IMPRINT",EDGE,{"derivedFrom":sQuery(id+"F1.wireOp",EDGE,"E16")}),1.0]])]});
            var Q1;
            Q1=makeQuery(id+"F1.imprint","IMPRINT",FACE,{"disambiguationData":[TD([[makeQuery(id+"F1.imprint","IMPRINT",EDGE,{"derivedFrom":sQuery(id+"F1.wireOp",EDGE,"E4")}),1.0]])]});
            var Q2;
            Q2=makeQuery(id+"F1.imprint","IMPRINT",FACE,{"disambiguationData":[TD([[makeQuery(id+"F1.imprint","IMPRINT",EDGE,{"derivedFrom":sQuery(id+"F1.wireOp",EDGE,"E7")}),1.0]])]});
            var Q3;
            Q3=makeQuery(id+"F1.imprint","IMPRINT",FACE,{"disambiguationData":[TD([[makeQuery(id+"F1.imprint","IMPRINT",EDGE,{"derivedFrom":sQuery(id+"F1.wireOp",EDGE,"E17")}),1.0]])]});
            var Q4;
            Q4=makeQuery(id+"F1.imprint","IMPRINT",FACE,{"disambiguationData":[TD([[makeQuery(id+"F1.imprint","IMPRINT",EDGE,{"derivedFrom":sQuery(id+"F1.wireOp",EDGE,"E5")}),1.0]])]});
            var Q5;
            Q5=makeQuery(id+"F1.imprint","IMPRINT",FACE,{"disambiguationData":[TD([[makeQuery(id+"F1.imprint","IMPRINT",EDGE,{"derivedFrom":sQuery(id+"F1.wireOp",EDGE,"E6")}),1.0]])]});
            extrude(context, id + "F9", {"entities" : qUnion([Q0, Q1, Q2, Q3, Q4, Q5]), "operationType" : NewBodyOperationType.REMOVE, "endBound" : BoundingType.SYMMETRIC, "depth" : 25 * mm});
        }
    });
